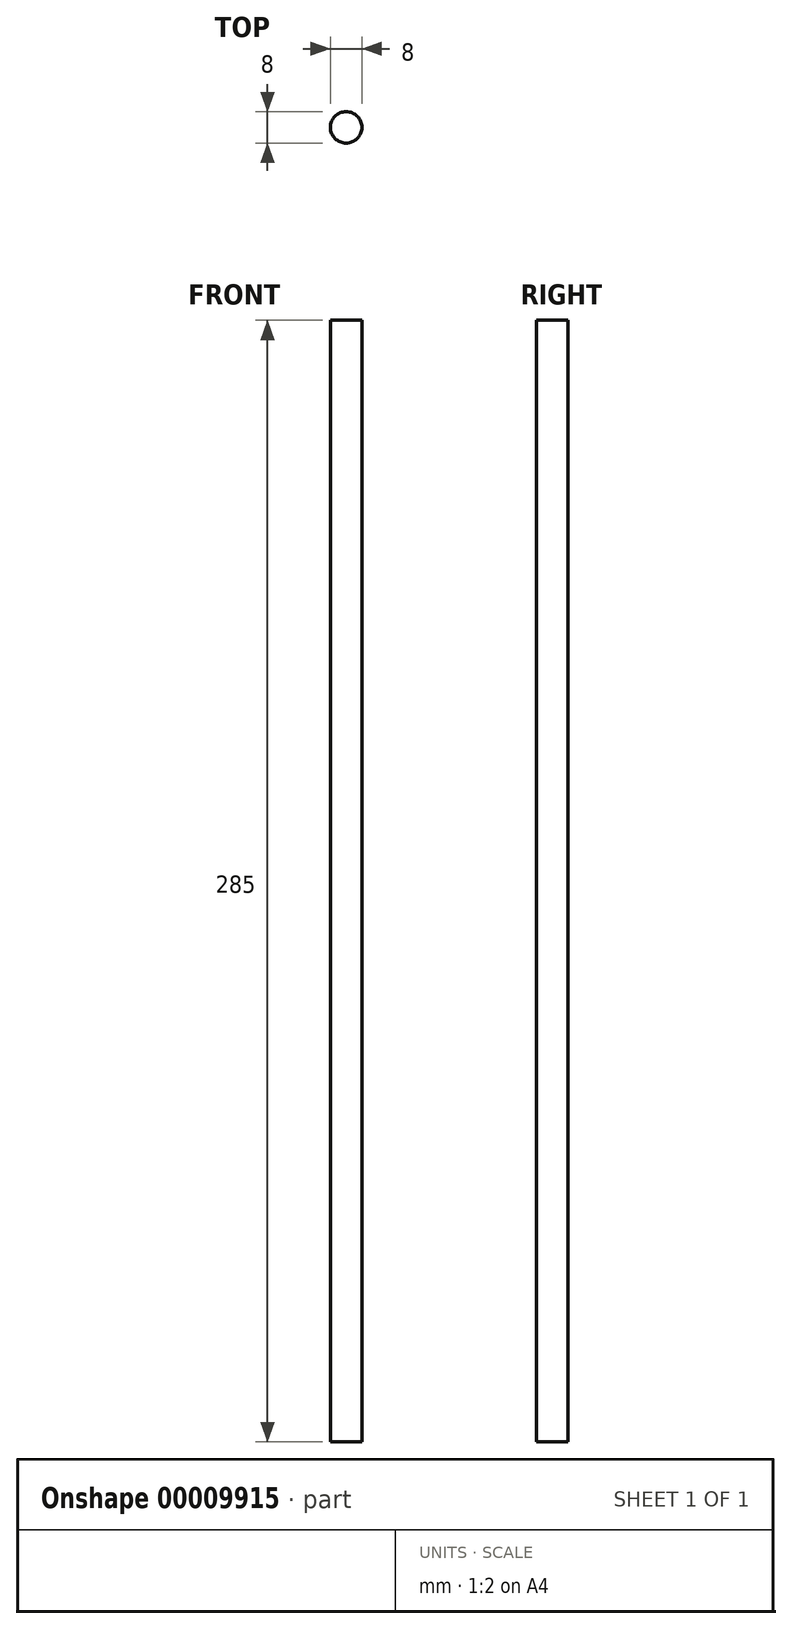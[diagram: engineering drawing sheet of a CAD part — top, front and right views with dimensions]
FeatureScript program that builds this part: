
annotation { "Feature Type Name" : "Feature", "Feature Type Description" : "" }
export const myFeature = defineFeature(function(context is Context, id is Id, definition is map)
    precondition{}
    {
        {
            var Q0;
            Q0=qCreatedBy(makeId("Top.planeOp"),FACE);
            var sketch = newSketch(context, id + "F0", { "sketchPlane" : qUnion([Q0])});
            skCircle(sketch, "E0", {"center": v(0, 0) * mm, "radius": 4 * mm});
            skSolve(sketch);
        }
        {
            var Q0;
            Q0 = qSketchRegion(id + "F0", true);
            extrude(context, id + "F1", {"entities" : qUnion([Q0]), "depth" : 285 * mm});
        }
    });
